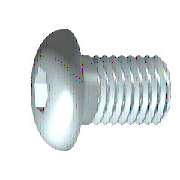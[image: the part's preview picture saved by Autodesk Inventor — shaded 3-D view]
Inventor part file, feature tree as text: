
AUTODESK INVENTOR PART (.ipt)
format: ipt  version: 2024.2 (Build 282272000, 272)  size: 199,680 bytes
history: native  units: mm (DEFAULTED — no unit token found)
features: extrude x1, plane x1, fillet x1
ambient origin geometry x7: Origin, YZ Plane, XY Plane, X Axis, Y Axis, Z Axis, Center Point
bodies: Solid1 (feature_tree), Body (feature_tree)
feature tree (3):
  extrude  "Slot"  Depth=13.6mm
  plane  "Work Plane1"
  fillet  "Fillet2"  Radius=0.49086mm
